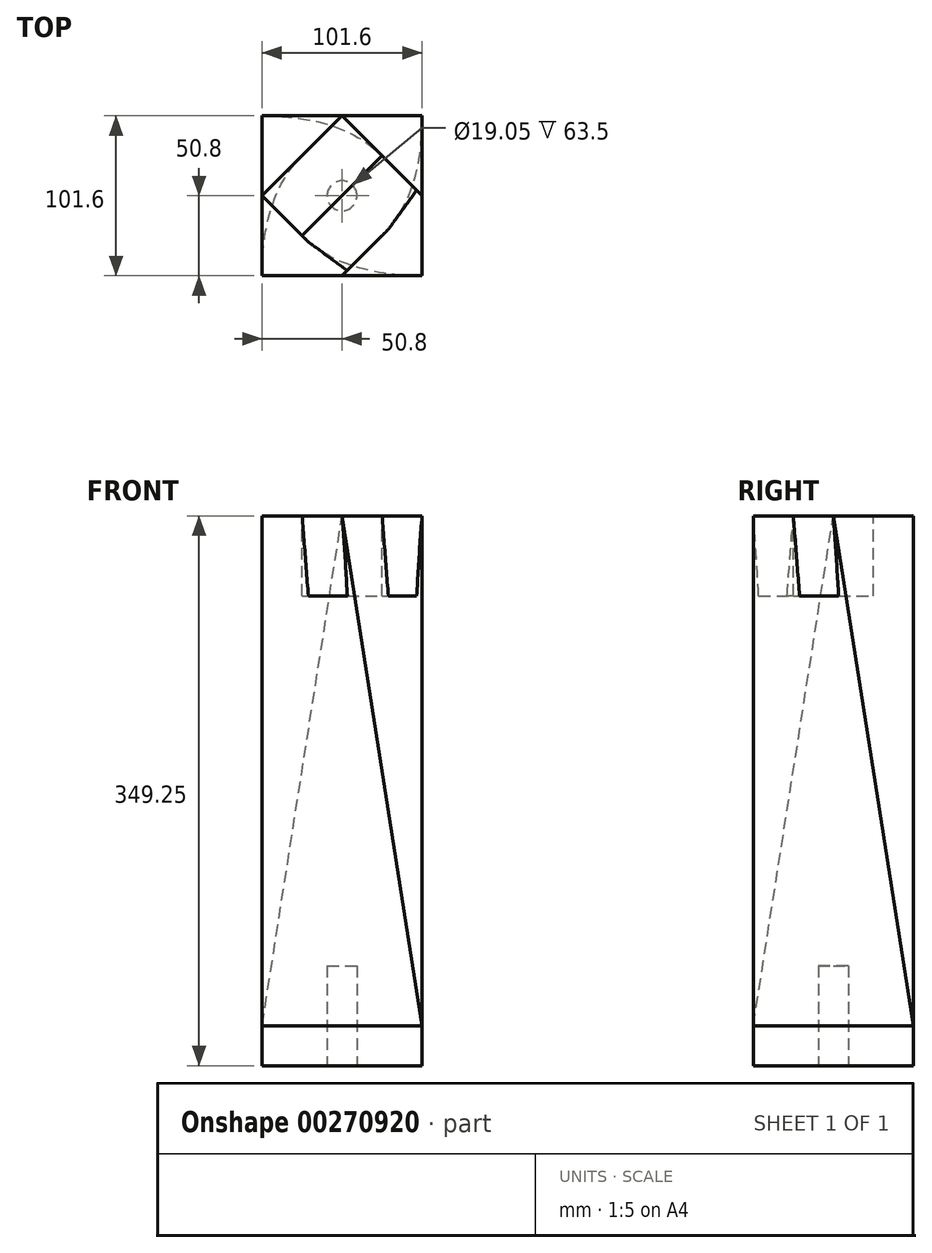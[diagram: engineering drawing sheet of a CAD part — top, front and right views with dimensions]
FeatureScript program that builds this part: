
annotation { "Feature Type Name" : "Feature", "Feature Type Description" : "" }
export const myFeature = defineFeature(function(context is Context, id is Id, definition is map)
    precondition{}
    {
        {
            var Q0;
            Q0=qCreatedBy(makeId("Front.planeOp"),FACE);
            var sketch = newSketch(context, id + "F0", { "sketchPlane" : qUnion([Q0])});
            skLineSegment(sketch, "E0", {"start": v(0, 0) * mm, "end": v(0, -25.4) * mm});
            skLineSegment(sketch, "E1", {"start": v(0, -25.4) * mm, "end": v(-101.6, -25.4) * mm});
            skLineSegment(sketch, "E2", {"start": v(-101.6, -25.4) * mm, "end": v(-101.6, 0) * mm});
            skLineSegment(sketch, "E3", {"start": v(-101.6, 0) * mm, "end": v(0, 0) * mm});
            skSolve(sketch);
        }
        {
            var Q0;
            Q0 = qSketchRegion(id + "F0", true);
            extrude(context, id + "F1", {"entities" : qUnion([Q0]), "depth" : 101.6 * mm});
        }
        {
            var Q0;
            Q0=makeQuery(id+"F1.opExtrude","SWEPT_FACE",FACE,{"disambiguationData":[OSD([sQuery(id+"F0.wireOp",EDGE,"E3")])]});
            cPlane(context, id + "F2", {"entities" : qUnion([Q0]), "cplaneType" : CPlaneType.OFFSET, "offset" : 323.85 * mm, "width" : 152.4 * mm, "height" : 152.4 * mm});
        }
        {
            var Q0;
            Q0=qCreatedBy(id+"F2.planeOp",FACE);
            var sketch = newSketch(context, id + "F3", { "sketchPlane" : qUnion([Q0])});
            skPoint(sketch, "E4.1", {"position": v(0, -50.8) * mm});
            skLineSegment(sketch, "E5", {"start": v(-50.8, 0) * mm, "end": v(-101.6, -50.8) * mm});
            skLineSegment(sketch, "E6", {"start": v(-101.6, -50.8) * mm, "end": v(-50.8, -101.6) * mm});
            skLineSegment(sketch, "E7", {"start": v(-50.8, -101.6) * mm, "end": v(0, -50.8) * mm});
            skLineSegment(sketch, "E8", {"start": v(-50.8, 0) * mm, "end": v(0, -50.8) * mm});
            skSolve(sketch);
        }
        {
            var Q1;
            Q1=makeQuery(id+"F1.opExtrude","SWEPT_FACE",FACE,{"disambiguationData":[OSD([sQuery(id+"F0.wireOp",EDGE,"E3")])]});
            var Q2;
            Q2=makeQuery(id+"F3.imprint","IMPRINT",FACE,{"disambiguationData":[TD([[makeQuery(id+"F3.imprint","IMPRINT",EDGE,{"derivedFrom":sQuery(id+"F3.wireOp",EDGE,"E5")}),1.0]])]});
            loft(context, id + "F4", {"operationType" : NewBodyOperationType.ADD, "sheetProfilesArray" : [{ "sheetProfileEntities" : qUnion([Q1]) }, { "sheetProfileEntities" : qUnion([Q2]) }]});
        }
        {
            var Q0;
            Q0=makeQuery(id+"F4.opLoft","CAP_FACE",FACE,{"disambiguationData":[OSD([makeQuery(id+"F3.imprint","IMPRINT",FACE,{"disambiguationData":[TD([[makeQuery(id+"F3.imprint","IMPRINT",EDGE,{"derivedFrom":sQuery(id+"F3.wireOp",EDGE,"E5")}),1.0]])]})])],"isStart":true});
            var sketch = newSketch(context, id + "F5", { "sketchPlane" : qUnion([Q0])});
            skLineSegment(sketch, "E9", {"start": v(-76.2, -25.4) * mm, "end": v(-25.4, -76.2) * mm});
            skLineSegment(sketch, "E10", {"start": v(-76.2, -76.2) * mm, "end": v(-25.4, -25.4) * mm});
            skCircle(sketch, "E11", {"center": v(-50.8, -50.8) * mm, "radius": 6.35 * mm});
            skPoint(sketch, "E11.perimeterSnap0", {"position": v(-50.8, -50.8) * mm});
            skSolve(sketch);
        }
        {
            var Q0;
            {var subQ0=sQuery(id+"F5.wireOp",EDGE,"E11");var subQ1=sQuery(id+"F5.wireOp",EDGE,"E9");var subQ2=makeQuery(id+"F5.imprint","INTERSECT",VERTEX,{"disambiguationData":[OD(0.0)],"derivedFrom":[subQ1,subQ0]});Q0=makeQuery(id+"F5.imprint","IMPRINT",FACE,{"disambiguationData":[TD([[makeQuery(id+"F5.imprint","IMPRINT",EDGE,{"disambiguationData":[TD([[subQ2,-1.0]])],"derivedFrom":subQ1}),1.0]])]});}
            var Q1;
            {var subQ0=sQuery(id+"F5.wireOp",EDGE,"E11");var subQ1=sQuery(id+"F5.wireOp",EDGE,"E9");var subQ2=makeQuery(id+"F5.imprint","INTERSECT",VERTEX,{"disambiguationData":[OD(0.0)],"derivedFrom":[subQ1,subQ0]});Q1=makeQuery(id+"F5.imprint","IMPRINT",FACE,{"disambiguationData":[TD([[makeQuery(id+"F5.imprint","IMPRINT",EDGE,{"disambiguationData":[TD([[subQ2,-1.0]])],"derivedFrom":subQ1}),-1.0]])]});}
            var Q2;
            {var subQ0=sQuery(id+"F5.wireOp",EDGE,"E10");var subQ1=sQuery(id+"F5.wireOp",EDGE,"E9");var subQ2=makeQuery(id+"F5.imprint","INTERSECT",VERTEX,{"derivedFrom":[subQ1,subQ0]});Q2=makeQuery(id+"F5.imprint","IMPRINT",FACE,{"disambiguationData":[TD([[makeQuery(id+"F5.imprint","IMPRINT",EDGE,{"disambiguationData":[TD([[subQ2,-1.0]])],"derivedFrom":subQ1}),-1.0]])]});}
            var Q3;
            {var subQ0=sQuery(id+"F5.wireOp",EDGE,"E10");var subQ1=sQuery(id+"F5.wireOp",EDGE,"E9");var subQ2=makeQuery(id+"F5.imprint","INTERSECT",VERTEX,{"derivedFrom":[subQ1,subQ0]});Q3=makeQuery(id+"F5.imprint","IMPRINT",FACE,{"disambiguationData":[TD([[makeQuery(id+"F5.imprint","IMPRINT",EDGE,{"disambiguationData":[TD([[subQ2,-1.0]])],"derivedFrom":subQ1}),1.0]])]});}
            extrude(context, id + "F6", {"entities" : qUnion([Q0, Q1, Q2, Q3]), "operationType" : NewBodyOperationType.REMOVE, "oppositeDirection" : true, "depth" : 50.8 * mm});
        }
        {
            var Q0;
            Q0=makeQuery(id+"F1.opExtrude","SWEPT_FACE",FACE,{"disambiguationData":[OSD([sQuery(id+"F0.wireOp",EDGE,"E1")])]});
            var sketch = newSketch(context, id + "F7", { "sketchPlane" : qUnion([Q0])});
            skLineSegment(sketch, "E12", {"start": v(-50.8, 101.6) * mm, "end": v(-50.8, 0) * mm});
            skCircle(sketch, "E13", {"center": v(-50.8, 50.8) * mm, "radius": 9.53 * mm});
            skSolve(sketch);
        }
        {
            var Q0;
            Q0 = qSketchRegion(id + "F7", true);
            extrude(context, id + "F8", {"entities" : qUnion([Q0]), "operationType" : NewBodyOperationType.REMOVE, "oppositeDirection" : true, "depth" : 63.5 * mm});
        }
    });
